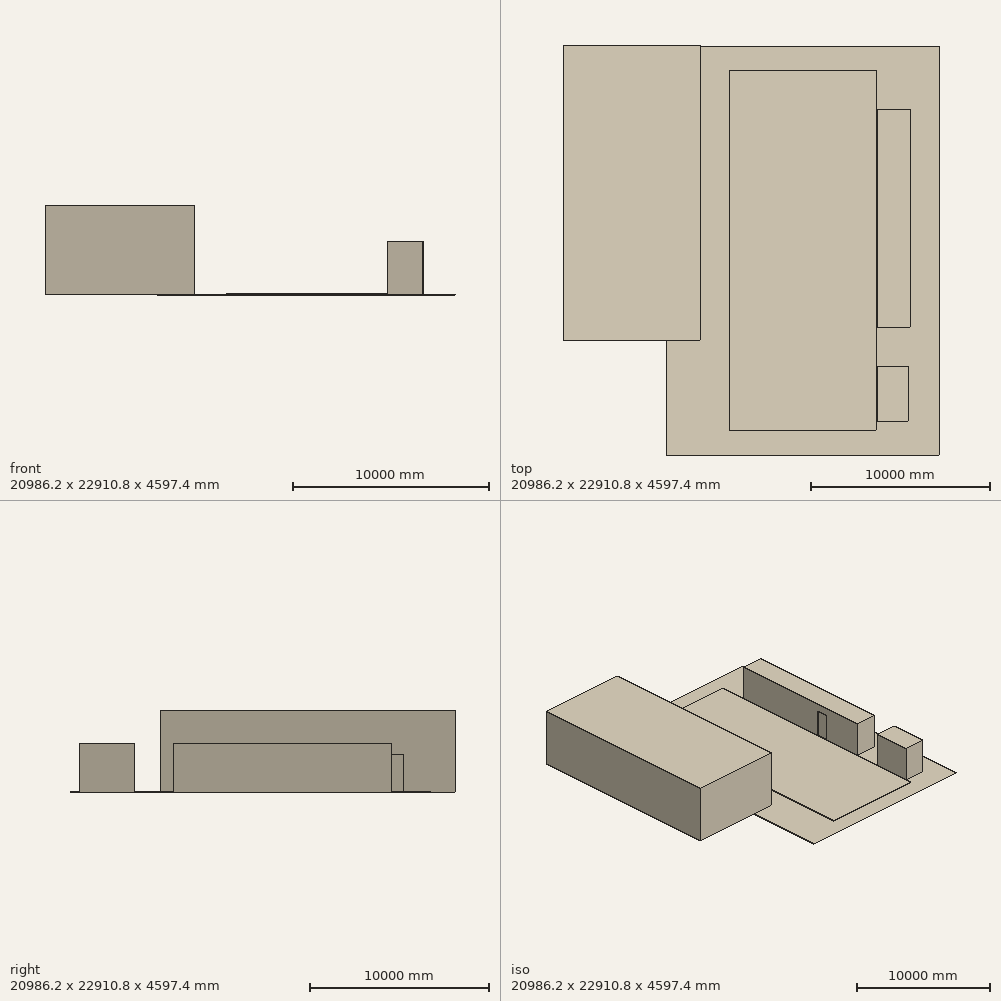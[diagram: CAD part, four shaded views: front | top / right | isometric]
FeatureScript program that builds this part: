
annotation { "Feature Type Name" : "Feature", "Feature Type Description" : "" }
export const myFeature = defineFeature(function(context is Context, id is Id, definition is map)
    precondition{}
    {
        {
            var Q0;
            Q0=qCreatedBy(makeId("Top.planeOp"),FACE);
            var sketch = newSketch(context, id + "F0", { "sketchPlane" : qUnion([Q0])});
            skLineSegment(sketch, "E0.bottom", {"start": v(-7620, 11430) * mm, "end": v(7620, 11430) * mm});
            skLineSegment(sketch, "E0.top", {"start": v(-7620, -11430) * mm, "end": v(7620, -11430) * mm});
            skLineSegment(sketch, "E0.left", {"start": v(-7620, 11430) * mm, "end": v(-7620, -11430) * mm});
            skLineSegment(sketch, "E0.right", {"start": v(7620, 11430) * mm, "end": v(7620, -11430) * mm});
            skSolve(sketch);
        }
        {
            var Q0;
            Q0=makeQuery(id+"F0.imprint","IMPRINT",FACE,{"disambiguationData":[TD([[makeQuery(id+"F0.imprint","IMPRINT",EDGE,{"derivedFrom":sQuery(id+"F0.wireOp",EDGE,"E0.bottom")}),-1.0]])]});
            extrude(context, id + "F1", {"entities" : qUnion([Q0]), "depth" : 25.4 * mm});
        }
        {
            var Q0;
            Q0=makeQuery(id+"F1.opExtrude","CAP_FACE",FACE,{"disambiguationData":[OSD([sQuery(id+"F0.wireOp",EDGE,"E0.bottom"),sQuery(id+"F0.wireOp",EDGE,"E0.top"),sQuery(id+"F0.wireOp",EDGE,"E0.left"),sQuery(id+"F0.wireOp",EDGE,"E0.right")])],"isStart":false});
            var sketch = newSketch(context, id + "F2", { "sketchPlane" : qUnion([Q0])});
            skLineSegment(sketch, "E1.bottom", {"start": v(-4114.8, 10058.4) * mm, "end": v(4114.8, 10058.4) * mm});
            skLineSegment(sketch, "E1.top", {"start": v(-4114.8, -10058.4) * mm, "end": v(4114.8, -10058.4) * mm});
            skLineSegment(sketch, "E1.left", {"start": v(-4114.8, 10058.4) * mm, "end": v(-4114.8, -10058.4) * mm});
            skLineSegment(sketch, "E1.right", {"start": v(4114.8, 10058.4) * mm, "end": v(4114.8, -10058.4) * mm});
            skSolve(sketch);
        }
        {
            var Q0;
            Q0=makeQuery(id+"F2.imprint","IMPRINT",FACE,{"disambiguationData":[TD([[makeQuery(id+"F2.imprint","IMPRINT",EDGE,{"derivedFrom":sQuery(id+"F2.wireOp",EDGE,"E1.bottom")}),-1.0]])]});
            extrude(context, id + "F3", {"entities" : qUnion([Q0]), "operationType" : NewBodyOperationType.ADD, "depth" : 50.8 * mm});
        }
        {
            var Q0;
            Q0=makeQuery(id+"F1.opExtrude","CAP_FACE",FACE,{"disambiguationData":[OSD([sQuery(id+"F0.wireOp",EDGE,"E0.bottom"),sQuery(id+"F0.wireOp",EDGE,"E0.top"),sQuery(id+"F0.wireOp",EDGE,"E0.left"),sQuery(id+"F0.wireOp",EDGE,"E0.right")])],"isStart":false});
            var sketch = newSketch(context, id + "F4", { "sketchPlane" : qUnion([Q0])});
            skLineSegment(sketch, "E2.bottom", {"start": v(4140.2, -6476.85) * mm, "end": v(5925.13, -6476.85) * mm});
            skLineSegment(sketch, "E2.top", {"start": v(4140.2, -9524.85) * mm, "end": v(5925.13, -9524.85) * mm});
            skLineSegment(sketch, "E2.left", {"start": v(4140.2, -6476.85) * mm, "end": v(4140.2, -9524.85) * mm});
            skLineSegment(sketch, "E2.right", {"start": v(5925.13, -6476.85) * mm, "end": v(5925.13, -9524.85) * mm});
            skSolve(sketch);
        }
        {
            var Q0;
            Q0=makeQuery(id+"F4.imprint","IMPRINT",FACE,{"disambiguationData":[TD([[makeQuery(id+"F4.imprint","IMPRINT",EDGE,{"derivedFrom":sQuery(id+"F4.wireOp",EDGE,"E2.bottom")}),-1.0]])]});
            extrude(context, id + "F5", {"entities" : qUnion([Q0]), "operationType" : NewBodyOperationType.ADD, "depth" : 2743.2 * mm});
        }
        {
            var Q0;
            Q0=makeQuery(id+"F1.opExtrude","CAP_FACE",FACE,{"disambiguationData":[OSD([sQuery(id+"F0.wireOp",EDGE,"E0.bottom"),sQuery(id+"F0.wireOp",EDGE,"E0.top"),sQuery(id+"F0.wireOp",EDGE,"E0.left"),sQuery(id+"F0.wireOp",EDGE,"E0.right")])],"isStart":false});
            var sketch = newSketch(context, id + "F6", { "sketchPlane" : qUnion([Q0])});
            skLineSegment(sketch, "E3.bottom", {"start": v(5994.4, 7899.55) * mm, "end": v(4165.6, 7899.55) * mm});
            skLineSegment(sketch, "E3.top", {"start": v(5994.4, -4292.45) * mm, "end": v(4165.6, -4292.45) * mm});
            skLineSegment(sketch, "E3.left", {"start": v(5994.4, 7899.55) * mm, "end": v(5994.4, -4292.45) * mm});
            skLineSegment(sketch, "E3.right", {"start": v(4165.6, 7899.55) * mm, "end": v(4165.6, -4292.45) * mm});
            skSolve(sketch);
        }
        {
            var Q0;
            Q0=makeQuery(id+"F6.imprint","IMPRINT",FACE,{"disambiguationData":[TD([[makeQuery(id+"F6.imprint","IMPRINT",EDGE,{"derivedFrom":sQuery(id+"F6.wireOp",EDGE,"E3.bottom")}),1.0]])]});
            extrude(context, id + "F7", {"entities" : qUnion([Q0]), "operationType" : NewBodyOperationType.ADD, "depth" : 2743.2 * mm});
        }
        {
            var Q0;
            Q0=makeQuery(id+"F1.opExtrude","CAP_FACE",FACE,{"disambiguationData":[OSD([sQuery(id+"F0.wireOp",EDGE,"E0.bottom"),sQuery(id+"F0.wireOp",EDGE,"E0.top"),sQuery(id+"F0.wireOp",EDGE,"E0.left"),sQuery(id+"F0.wireOp",EDGE,"E0.right")])],"isStart":false});
            var sketch = newSketch(context, id + "F8", { "sketchPlane" : qUnion([Q0])});
            skSolve(sketch);
        }
        {
            var Q0;
            Q0=makeQuery(id+"F8.imprint","IMPRINT",FACE,{"disambiguationData":[TD([[makeQuery(id+"F8.imprint","IMPRINT",EDGE,{"derivedFrom":makeQuery(id+"F1.opExtrude","CAP_EDGE",EDGE,{"disambiguationData":[OSD([sQuery(id+"F0.wireOp",EDGE,"E0.bottom")])],"isStart":false})}),-1.0]])]});
            var sketch = newSketch(context, id + "F9", { "sketchPlane" : qUnion([Q0])});
            skLineSegment(sketch, "E4.bottom", {"start": v(-13366.16, 11480.8) * mm, "end": v(-5746.16, 11480.8) * mm});
            skLineSegment(sketch, "E4.top", {"start": v(-13366.16, -5029.2) * mm, "end": v(-5746.16, -5029.2) * mm});
            skLineSegment(sketch, "E4.left", {"start": v(-13366.16, 11480.8) * mm, "end": v(-13366.16, -5029.2) * mm});
            skLineSegment(sketch, "E4.right", {"start": v(-5746.16, 11480.8) * mm, "end": v(-5746.16, -5029.2) * mm});
            skSolve(sketch);
        }
        {
            var Q0;
            {var subQ1=sQuery(id+"F9.wireOp",EDGE,"E4.bottom");Q0=makeQuery(id+"F9.imprint","IMPRINT",FACE,{"disambiguationData":[TD([[makeQuery(id+"F9.imprint","IMPRINT",EDGE,{"derivedFrom":subQ1}),-1.0]])]});}
            var Q1;
            {var subQ0=sQuery(id+"F9.wireOp",EDGE,"E4.right");var subQ1=sQuery(id+"F9.wireOp",EDGE,"E4.top");var subQ2=makeQuery(id+"F9.imprint","INTERSECT",VERTEX,{"derivedFrom":[subQ1,subQ0]});Q1=makeQuery(id+"F9.imprint","IMPRINT",FACE,{"disambiguationData":[TD([[makeQuery(id+"F9.imprint","IMPRINT",EDGE,{"disambiguationData":[TD([[subQ2,1.0]])],"derivedFrom":subQ1}),1.0]])]});}
            extrude(context, id + "F10", {"entities" : qUnion([Q0, Q1]), "operationType" : NewBodyOperationType.ADD, "depth" : 4572 * mm});
        }
        {
            var Q0;
            Q0=makeQuery(id+"F10.opExtrude","SWEPT_FACE",FACE,{"disambiguationData":[OSD([sQuery(id+"F9.wireOp",EDGE,"E4.right")])]});
            var sketch = newSketch(context, id + "F11", { "sketchPlane" : qUnion([Q0])});
            skLineSegment(sketch, "E5.bottom", {"start": v(-3759.2, 2159) * mm, "end": v(-2844.8, 2159) * mm});
            skLineSegment(sketch, "E5.top", {"start": v(-3759.2, 25.4) * mm, "end": v(-2844.8, 25.4) * mm});
            skLineSegment(sketch, "E5.left", {"start": v(-3759.2, 2159) * mm, "end": v(-3759.2, 25.4) * mm});
            skLineSegment(sketch, "E5.right", {"start": v(-2844.8, 2159) * mm, "end": v(-2844.8, 25.4) * mm});
            skLineSegment(sketch, "E6.bottom", {"start": v(7641.18, 2159) * mm, "end": v(8555.58, 2159) * mm});
            skLineSegment(sketch, "E6.top", {"start": v(7641.18, 25.4) * mm, "end": v(8555.58, 25.4) * mm});
            skLineSegment(sketch, "E6.left", {"start": v(7641.18, 2159) * mm, "end": v(7641.18, 25.4) * mm});
            skLineSegment(sketch, "E6.right", {"start": v(8555.58, 2159) * mm, "end": v(8555.58, 25.4) * mm});
            skSolve(sketch);
        }
        {
            var Q0;
            Q0=makeQuery(id+"F11.imprint","IMPRINT",FACE,{"disambiguationData":[TD([[makeQuery(id+"F11.imprint","IMPRINT",EDGE,{"derivedFrom":sQuery(id+"F11.wireOp",EDGE,"E5.bottom")}),-1.0]])]});
            var Q1;
            Q1=makeQuery(id+"F11.imprint","IMPRINT",FACE,{"disambiguationData":[TD([[makeQuery(id+"F11.imprint","IMPRINT",EDGE,{"derivedFrom":sQuery(id+"F11.wireOp",EDGE,"E6.bottom")}),-1.0]])]});
            extrude(context, id + "F12", {"entities" : qUnion([Q0, Q1]), "operationType" : NewBodyOperationType.REMOVE, "oppositeDirection" : true, "depth" : 76.2 * mm});
        }
        {
            var Q0;
            Q0=makeQuery(id+"F7.opExtrude","SWEPT_FACE",FACE,{"disambiguationData":[OSD([sQuery(id+"F6.wireOp",EDGE,"E3.right")])]});
            var sketch = newSketch(context, id + "F13", { "sketchPlane" : qUnion([Q0])});
            skLineSegment(sketch, "E7.bottom", {"start": v(0, 2159) * mm, "end": v(914.4, 2159) * mm});
            skLineSegment(sketch, "E7.top", {"start": v(0, 25.4) * mm, "end": v(914.4, 25.4) * mm});
            skLineSegment(sketch, "E7.left", {"start": v(0, 2159) * mm, "end": v(0, 25.4) * mm});
            skLineSegment(sketch, "E7.right", {"start": v(914.4, 2159) * mm, "end": v(914.4, 25.4) * mm});
            skSolve(sketch);
        }
        {
            var Q0;
            Q0=makeQuery(id+"F13.imprint","IMPRINT",FACE,{"disambiguationData":[TD([[makeQuery(id+"F13.imprint","IMPRINT",EDGE,{"derivedFrom":sQuery(id+"F13.wireOp",EDGE,"E7.bottom")}),-1.0]])]});
            extrude(context, id + "F14", {"entities" : qUnion([Q0]), "operationType" : NewBodyOperationType.REMOVE, "oppositeDirection" : true, "depth" : 76.2 * mm});
        }
    });
